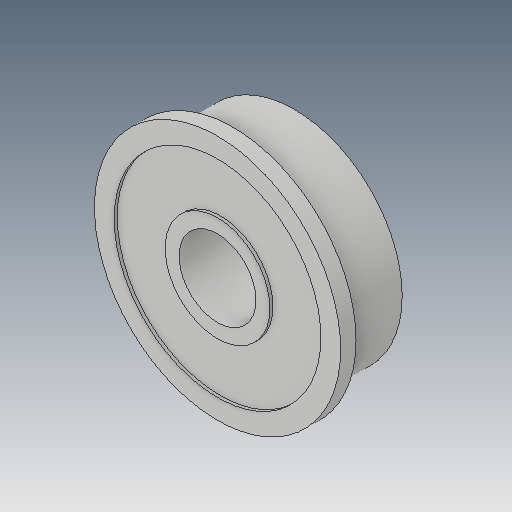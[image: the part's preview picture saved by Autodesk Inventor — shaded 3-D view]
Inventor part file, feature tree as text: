
AUTODESK INVENTOR PART (.ipt)
format: ipt  version: 2017 (Build 210142000, 142)  size: 152,576 bytes
history: native  units: mm
features: other x5, extrude x3, sketch x3, reference x2
ambient origin geometry x8: Origin, YZ Plane, XZ Plane, XY Plane, X Axis, Y Axis, Z Axis, Center Point
bodies: Solid1 (feature_tree)
feature tree (13):
  extrude  "Extrusion1"  Depth=5.0mm
  extrude  "Extrusion2"  Depth=5.0mm
  extrude  "Extrusion3"  Depth=0.2mm TaperAngle=0.0deg
  sketch  "Sketch1"  dims[d0=5.0mm d1=14.0mm]
  reference  "Reference1"
  sketch  "Sketch2"  dims[d2=5.0mm d3=0.0mm d4=16.0mm]
  sketch  "Sketch3"  dims[d5=1.0mm d6=0.0mm d7=0.2mm d8=0.0mm]
  reference  "Reference2"
  other  "<userpath>\OneDrive\SL-Inventor\SL-Beast 3D Printer\x-aXIS-aSSEMBLY.iam"
  other  "x-aXIS-aSSEMBLY.iam"
  other  "Washer:1"
  parser-record x1  (decoder bookkeeping rows leaked as tree rows — omitted from the tree; the rows remain in map.json)
  other  "Forged Socket Head Cap Screw - Metric M5x0.8 x 25:1"
note: 1 file-system path scrubbed to <path> (originals preserved in map.json)
